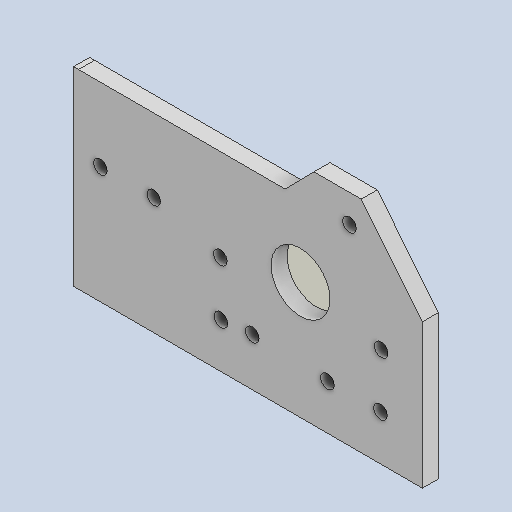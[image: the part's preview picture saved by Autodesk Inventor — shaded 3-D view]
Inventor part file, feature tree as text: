
AUTODESK INVENTOR PART (.ipt)
format: ipt  version: 2023.2 (Build 272271000, 271)  size: 359,424 bytes
history: native  units: mm
features: reference x17, other x3, sketch x2, plane x1, extrude x1, hole x1
ambient origin geometry x8: Origin, YZ Plane, XZ Plane, XY Plane, X Axis, Y Axis, Z Axis, Center Point
bodies: Solid1 (feature_tree)
feature tree (25):
  plane  "Work Plane1"
  extrude  "Extrusion1"  Depth=6.0mm
  hole  "Hole1"  [1 undecoded]
  sketch  "Sketch1"  dims[d2=110.0mm]
  reference  "Reference1"
  reference  "Reference2"
  reference  "Reference3"
  reference  "Reference4"
  reference  "Reference5"
  reference  "Reference6"
  reference  "Reference7"
  reference  "Reference8"
  reference  "Reference9"
  reference  "Reference10"
  reference  "Reference11"
  reference  "Reference12"
  reference  "Reference13"
  reference  "Reference14"
  reference  "Reference15"
  reference  "Reference16"
  reference  "Reference17"
  sketch  "Sketch2"  dims[d3=5.1mm d4=5.1mm d5=5.1mm d7=7.0mm d8=7.0mm d9=7.0mm d10=3.0mm d11=20.0mm d12=22.1mm d13=6.0mm d14=0.0mm d16=5.1mm d17=6.0mm d18=4.0mm d19=2.0mm d20=90.0deg d21=8.0mm d22=20.594885mm d30=15.0mm d33=54.0mm d36=20.0mm d37=15.000003mm]
  parser-record x1  (decoder bookkeeping rows leaked as tree rows — omitted from the tree; the rows remain in map.json)
  other  "Main Assembly.iam"
  other  "C beam extrusion 460:1"
note: 1 required parameter value undecoded (feature->parameter linkage not recoverable at this tier; creation-order binding heuristic only, values carry confidence <= 0.55)
note: 1 file-system path scrubbed to <path> (originals preserved in map.json)
